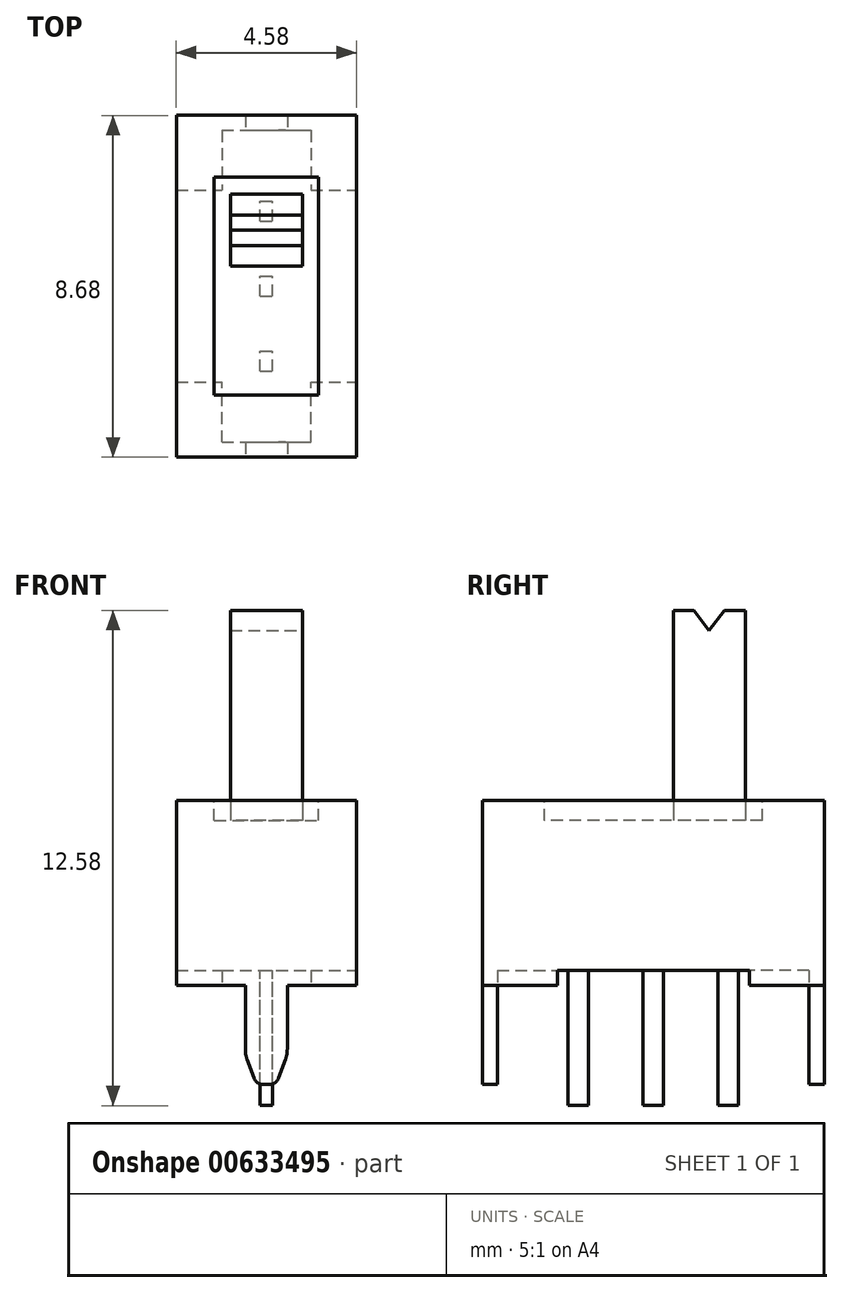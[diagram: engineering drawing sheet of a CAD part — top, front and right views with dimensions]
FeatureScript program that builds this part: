
annotation { "Feature Type Name" : "Feature", "Feature Type Description" : "" }
export const myFeature = defineFeature(function(context is Context, id is Id, definition is map)
    precondition{}
    {
        {
            var Q0;
            Q0=qCreatedBy(makeId("Top.planeOp"),FACE);
            var sketch = newSketch(context, id + "F0", { "sketchPlane" : qUnion([Q0])});
            skLineSegment(sketch, "E0.bottom", {"start": v(2.29, 4.34) * mm, "end": v(-2.29, 4.34) * mm});
            skLineSegment(sketch, "E0.top", {"start": v(2.29, -4.34) * mm, "end": v(-2.29, -4.34) * mm});
            skLineSegment(sketch, "E0.left", {"start": v(2.29, 4.34) * mm, "end": v(2.29, -4.34) * mm});
            skLineSegment(sketch, "E0.right", {"start": v(-2.29, 4.34) * mm, "end": v(-2.29, -4.34) * mm});
            skLineSegment(sketch, "E1", {"start": v(2.29, 4.34) * mm, "end": v(-2.29, -4.34) * mm, "construction": true});
            skSolve(sketch);
        }
        {
            var Q0;
            Q0 = qSketchRegion(id + "F0", true);
            var Q1;
            Q1=makeQuery(id+"F0.imprint","IMPRINT",FACE,{"disambiguationData":[TD([[makeQuery(id+"F0.imprint","IMPRINT",EDGE,{"derivedFrom":sQuery(id+"F0.wireOp",EDGE,"E0.bottom")}),1.0]])]});
            extrude(context, id + "F1", {"entities" : qUnion([Q0, Q1]), "endBound" : BoundingType.SYMMETRIC, "depth" : 4.7 * mm, "offsetDistance" : 25.4 * mm});
        }
        {
            var Q0;
            Q0=makeQuery(id+"F1.opExtrude","CAP_FACE",FACE,{"disambiguationData":[OSD([sQuery(id+"F0.wireOp",EDGE,"E0.bottom"),sQuery(id+"F0.wireOp",EDGE,"E0.top"),sQuery(id+"F0.wireOp",EDGE,"E0.left"),sQuery(id+"F0.wireOp",EDGE,"E0.right")])],"isStart":false});
            var sketch = newSketch(context, id + "F2", { "sketchPlane" : qUnion([Q0])});
            skLineSegment(sketch, "E2.bottom", {"start": v(-1.32, 2.77) * mm, "end": v(1.32, 2.77) * mm});
            skLineSegment(sketch, "E2.top", {"start": v(-1.32, -2.77) * mm, "end": v(1.32, -2.77) * mm});
            skLineSegment(sketch, "E2.left", {"start": v(-1.32, 2.77) * mm, "end": v(-1.32, -2.77) * mm});
            skLineSegment(sketch, "E2.right", {"start": v(1.32, 2.77) * mm, "end": v(1.32, -2.77) * mm});
            skLineSegment(sketch, "E3", {"start": v(1.32, 2.77) * mm, "end": v(-1.32, -2.77) * mm, "construction": true});
            skSolve(sketch);
        }
        {
            var Q0;
            Q0 = qSketchRegion(id + "F2", true);
            extrude(context, id + "F3", {"entities" : qUnion([Q0]), "operationType" : NewBodyOperationType.REMOVE, "oppositeDirection" : true, "depth" : 0.5 * mm, "offsetDistance" : 25.4 * mm});
        }
        {
            var Q0;
            Q0=makeQuery(id+"F1.opExtrude","CAP_FACE",FACE,{"disambiguationData":[OSD([sQuery(id+"F0.wireOp",EDGE,"E0.bottom"),sQuery(id+"F0.wireOp",EDGE,"E0.top"),sQuery(id+"F0.wireOp",EDGE,"E0.left"),sQuery(id+"F0.wireOp",EDGE,"E0.right")])],"isStart":true});
            var sketch = newSketch(context, id + "F4", { "sketchPlane" : qUnion([Q0])});
            skLineSegment(sketch, "E4.bottom", {"start": v(-0.91, -0.5) * mm, "end": v(0.91, -0.5) * mm});
            skLineSegment(sketch, "E4.top", {"start": v(-0.91, -2.34) * mm, "end": v(0.91, -2.34) * mm});
            skLineSegment(sketch, "E4.left", {"start": v(-0.91, -0.5) * mm, "end": v(-0.91, -2.34) * mm});
            skLineSegment(sketch, "E4.right", {"start": v(0.91, -0.5) * mm, "end": v(0.91, -2.34) * mm});
            skLineSegment(sketch, "E5", {"start": v(0, 0) * mm, "end": v(0, -0.5) * mm, "construction": true});
            skSolve(sketch);
        }
        {
            var Q0;
            Q0 = qSketchRegion(id + "F4", true);
            extrude(context, id + "F5", {"entities" : qUnion([Q0]), "operationType" : NewBodyOperationType.ADD, "oppositeDirection" : true, "depth" : 9.52 * mm, "offsetDistance" : 25.4 * mm});
        }
        {
            var Q0;
            Q0=qCreatedBy(makeId("Right.planeOp"),FACE);
            var sketch = newSketch(context, id + "F6", { "sketchPlane" : qUnion([Q0])});
            skLineSegment(sketch, "E6", {"start": v(1.42, 7.18) * mm, "end": v(1.42, 13.06) * mm, "construction": true});
            skLineSegment(sketch, "E7", {"start": v(1.03, 7.18) * mm, "end": v(1.81, 7.18) * mm});
            skLineSegment(sketch, "E8", {"start": v(1.81, 7.18) * mm, "end": v(1.42, 6.67) * mm});
            skLineSegment(sketch, "E9", {"start": v(1.42, 6.67) * mm, "end": v(1.03, 7.18) * mm});
            skSolve(sketch);
        }
        {
            var Q0;
            Q0 = qSketchRegion(id + "F6", true);
            extrude(context, id + "F7", {"entities" : qUnion([Q0]), "operationType" : NewBodyOperationType.REMOVE, "endBound" : BoundingType.SYMMETRIC, "oppositeDirection" : true, "depth" : 25.4 * mm, "offsetDistance" : 25.4 * mm});
        }
        {
            var Q0;
            Q0=makeQuery(id+"F1.opExtrude","CAP_FACE",FACE,{"disambiguationData":[OSD([sQuery(id+"F0.wireOp",EDGE,"E0.bottom"),sQuery(id+"F0.wireOp",EDGE,"E0.top"),sQuery(id+"F0.wireOp",EDGE,"E0.left"),sQuery(id+"F0.wireOp",EDGE,"E0.right")])],"isStart":true});
            var sketch = newSketch(context, id + "F8", { "sketchPlane" : qUnion([Q0])});
            skLineSegment(sketch, "E10", {"start": v(-1.82, 0) * mm, "end": v(7.05, 0) * mm, "construction": true});
            skLineSegment(sketch, "E11.bottom", {"start": v(-1.13, 3.96) * mm, "end": v(1.13, 3.96) * mm});
            skLineSegment(sketch, "E11.left", {"start": v(-1.13, 3.96) * mm, "end": v(-1.13, 2.44) * mm});
            skLineSegment(sketch, "E11.right", {"start": v(1.13, 3.96) * mm, "end": v(1.13, 2.44) * mm});
            skLineSegment(sketch, "E12.bottom", {"start": v(-2.29, 2.44) * mm, "end": v(-1.13, 2.44) * mm});
            skLineSegment(sketch, "E12.left", {"start": v(-2.29, 2.44) * mm, "end": v(-2.29, 0) * mm});
            skLineSegment(sketch, "E12.right", {"start": v(2.29, 2.44) * mm, "end": v(2.29, 0) * mm});
            skLineSegment(sketch, "E13.trimOffspring", {"start": v(1.13, 2.44) * mm, "end": v(2.29, 2.44) * mm});
            skLineSegment(sketch, "E14", {"start": v(0, 0) * mm, "end": v(0, 6.83) * mm, "construction": true});
            skLineSegment(sketch, "E15.MirrorCS", {"start": v(-2.29, -2.44) * mm, "end": v(-2.29, 0) * mm});
            skLineSegment(sketch, "E16.MirrorCS", {"start": v(-2.29, -2.44) * mm, "end": v(-1.13, -2.44) * mm});
            skLineSegment(sketch, "E17.MirrorCS", {"start": v(1.13, -3.96) * mm, "end": v(1.13, -2.44) * mm});
            skLineSegment(sketch, "E18.MirrorCS", {"start": v(-1.13, -3.96) * mm, "end": v(-1.13, -2.44) * mm});
            skLineSegment(sketch, "E19.MirrorCS", {"start": v(-1.13, -3.96) * mm, "end": v(1.13, -3.96) * mm});
            skLineSegment(sketch, "E20.MirrorCS", {"start": v(1.13, -2.44) * mm, "end": v(2.29, -2.44) * mm});
            skLineSegment(sketch, "E21.MirrorCS", {"start": v(2.29, -2.44) * mm, "end": v(2.29, 0) * mm});
            skSolve(sketch);
        }
        {
            var Q0;
            Q0 = qSketchRegion(id + "F8", true);
            extrude(context, id + "F9", {"entities" : qUnion([Q0]), "operationType" : NewBodyOperationType.REMOVE, "oppositeDirection" : true, "depth" : 0.38 * mm, "offsetDistance" : 25.4 * mm});
        }
        {
            var Q0;
            Q0=qCreatedBy(makeId("Front.planeOp"),FACE);
            var sketch = newSketch(context, id + "F10", { "sketchPlane" : qUnion([Q0])});
            skLineSegment(sketch, "E22.bottom", {"start": v(0.53, -2.35) * mm, "end": v(-0.53, -2.35) * mm});
            skLineSegment(sketch, "E22.top", {"start": v(0.08, -4.86) * mm, "end": v(-0.08, -4.86) * mm});
            skLineSegment(sketch, "E22.left", {"start": v(0.53, -2.35) * mm, "end": v(0.53, -3.97) * mm});
            skLineSegment(sketch, "E22.right", {"start": v(-0.53, -2.35) * mm, "end": v(-0.53, -3.97) * mm});
            skLineSegment(sketch, "E23", {"start": v(0, 0) * mm, "end": v(0, -2.35) * mm, "construction": true});
            skLineSegment(sketch, "E24", {"start": v(0.32, -4.7) * mm, "end": v(0.49, -4.23) * mm});
            skLineSegment(sketch, "E25.MirrorCS", {"start": v(-0.32, -4.7) * mm, "end": v(-0.49, -4.23) * mm});
            skPoint(sketch, "E26.orphan", {"position": v(-0.53, -4.86) * mm});
            skPoint(sketch, "E27.visualSharp", {"position": v(-0.53, -4.1) * mm});
            skArc(sketch, "E27.filletArc", {"start": v(-0.53, -3.97) * mm, "mid": v(-0.52, -4.1) * mm, "end": v(-0.49, -4.23) * mm});
            skPoint(sketch, "E28.visualSharp", {"position": v(-0.26, -4.86) * mm});
            skArc(sketch, "E28.filletArc", {"start": v(-0.32, -4.7) * mm, "mid": v(-0.22, -4.82) * mm, "end": v(-0.08, -4.86) * mm});
            skPoint(sketch, "E29.visualSharp", {"position": v(0.26, -4.86) * mm});
            skArc(sketch, "E29.filletArc", {"start": v(0.08, -4.86) * mm, "mid": v(0.22, -4.82) * mm, "end": v(0.32, -4.7) * mm});
            skPoint(sketch, "E30.visualSharp", {"position": v(0.53, -4.1) * mm});
            skArc(sketch, "E30.filletArc", {"start": v(0.49, -4.23) * mm, "mid": v(0.52, -4.1) * mm, "end": v(0.53, -3.97) * mm});
            skSolve(sketch);
        }
        {
            var Q0;
            Q0 = qSketchRegion(id + "F10", true);
            var Q1;
            Q1=makeQuery(id+"F1.opExtrude","SWEPT_FACE",FACE,{"disambiguationData":[OSD([sQuery(id+"F0.wireOp",EDGE,"E0.bottom")])]});
            var Q2;
            Q2=makeQuery(id+"F1.opExtrude","SWEPT_FACE",FACE,{"disambiguationData":[OSD([sQuery(id+"F0.wireOp",EDGE,"E0.top")])]});
            extrude(context, id + "F11", {"entities" : qUnion([Q0]), "operationType" : NewBodyOperationType.ADD, "endBound" : BoundingType.UP_TO_SURFACE, "oppositeDirection" : true, "depth" : 0.38 * mm, "endBoundEntityFace" : qUnion([Q1]), "offsetDistance" : 25.4 * mm, "hasSecondDirection" : true, "secondDirectionBound" : SecondDirectionBoundingType.UP_TO_SURFACE, "secondDirectionOppositeDirection" : false, "secondDirectionDepth" : 25.4 * mm, "secondDirectionBoundEntityFace" : qUnion([Q2])});
        }
        {
            var Q0;
            Q0=makeQuery(id+"F9.boolean.opBoolean","COPY",FACE,{"derivedFrom":makeQuery(id+"F9.opExtrude","CAP_FACE",FACE,{"disambiguationData":[OSD([sQuery(id+"F8.wireOp",EDGE,"E11.bottom"),sQuery(id+"F8.wireOp",EDGE,"E11.left"),sQuery(id+"F8.wireOp",EDGE,"E11.right"),sQuery(id+"F8.wireOp",EDGE,"E12.bottom"),sQuery(id+"F8.wireOp",EDGE,"E12.left"),sQuery(id+"F8.wireOp",EDGE,"E12.right"),sQuery(id+"F8.wireOp",EDGE,"E13.trimOffspring"),sQuery(id+"F8.wireOp",EDGE,"E15.MirrorCS"),sQuery(id+"F8.wireOp",EDGE,"E16.MirrorCS"),sQuery(id+"F8.wireOp",EDGE,"E17.MirrorCS"),sQuery(id+"F8.wireOp",EDGE,"E18.MirrorCS"),sQuery(id+"F8.wireOp",EDGE,"E19.MirrorCS"),sQuery(id+"F8.wireOp",EDGE,"E20.MirrorCS"),sQuery(id+"F8.wireOp",EDGE,"E21.MirrorCS")])],"isStart":false})});
            var sketch = newSketch(context, id + "F12", { "sketchPlane" : qUnion([Q0])});
            skLineSegment(sketch, "E31.bottom", {"start": v(1.13, 3.96) * mm, "end": v(-1.13, 3.96) * mm});
            skLineSegment(sketch, "E31.top", {"start": v(1.13, -3.96) * mm, "end": v(-1.13, -3.96) * mm});
            skLineSegment(sketch, "E31.left", {"start": v(1.13, 3.96) * mm, "end": v(1.13, -3.96) * mm});
            skLineSegment(sketch, "E31.right", {"start": v(-1.13, 3.96) * mm, "end": v(-1.13, -3.96) * mm});
            skSolve(sketch);
        }
        {
            var Q0;
            Q0 = qSketchRegion(id + "F12", true);
            extrude(context, id + "F13", {"entities" : qUnion([Q0]), "operationType" : NewBodyOperationType.REMOVE, "endBound" : BoundingType.THROUGH_ALL, "depth" : 25.4 * mm, "offsetDistance" : 25.4 * mm});
        }
        {
            var Q0;
            Q0=makeQuery(id+"F9.boolean.opBoolean","COPY",FACE,{"derivedFrom":makeQuery(id+"F9.opExtrude","CAP_FACE",FACE,{"disambiguationData":[OSD([sQuery(id+"F8.wireOp",EDGE,"E11.bottom"),sQuery(id+"F8.wireOp",EDGE,"E11.left"),sQuery(id+"F8.wireOp",EDGE,"E11.right"),sQuery(id+"F8.wireOp",EDGE,"E12.bottom"),sQuery(id+"F8.wireOp",EDGE,"E12.left"),sQuery(id+"F8.wireOp",EDGE,"E12.right"),sQuery(id+"F8.wireOp",EDGE,"E13.trimOffspring"),sQuery(id+"F8.wireOp",EDGE,"E15.MirrorCS"),sQuery(id+"F8.wireOp",EDGE,"E16.MirrorCS"),sQuery(id+"F8.wireOp",EDGE,"E17.MirrorCS"),sQuery(id+"F8.wireOp",EDGE,"E18.MirrorCS"),sQuery(id+"F8.wireOp",EDGE,"E19.MirrorCS"),sQuery(id+"F8.wireOp",EDGE,"E20.MirrorCS"),sQuery(id+"F8.wireOp",EDGE,"E21.MirrorCS")])],"isStart":false})});
            var sketch = newSketch(context, id + "F14", { "sketchPlane" : qUnion([Q0])});
            skLineSegment(sketch, "E32.bottom", {"start": v(-0.15, 2.16) * mm, "end": v(0.15, 2.16) * mm});
            skLineSegment(sketch, "E32.top", {"start": v(-0.15, 1.65) * mm, "end": v(0.15, 1.65) * mm});
            skLineSegment(sketch, "E32.left", {"start": v(-0.15, 2.16) * mm, "end": v(-0.15, 1.65) * mm});
            skLineSegment(sketch, "E32.right", {"start": v(0.15, 2.16) * mm, "end": v(0.15, 1.65) * mm});
            skLineSegment(sketch, "E33", {"start": v(0, 2.16) * mm, "end": v(0, -3.4) * mm, "construction": true});
            skLineSegment(sketch, "E34.1.0.0", {"start": v(0.15, 0.25) * mm, "end": v(0.15, -0.25) * mm});
            skLineSegment(sketch, "E34.1.0.1", {"start": v(-0.15, 0.25) * mm, "end": v(0.15, 0.25) * mm});
            skLineSegment(sketch, "E34.1.0.2", {"start": v(-0.15, -0.25) * mm, "end": v(0.15, -0.25) * mm});
            skLineSegment(sketch, "E34.1.0.3", {"start": v(-0.15, 0.25) * mm, "end": v(-0.15, -0.25) * mm});
            skLineSegment(sketch, "E34.2.0.0", {"start": v(0.15, -1.65) * mm, "end": v(0.15, -2.16) * mm});
            skLineSegment(sketch, "E34.2.0.1", {"start": v(-0.15, -1.65) * mm, "end": v(0.15, -1.65) * mm});
            skLineSegment(sketch, "E34.2.0.2", {"start": v(-0.15, -2.16) * mm, "end": v(0.15, -2.16) * mm});
            skLineSegment(sketch, "E34.2.0.3", {"start": v(-0.15, -1.65) * mm, "end": v(-0.15, -2.16) * mm});
            skLineSegment(sketch, "E34.direction1", {"start": v(-0.15, 1.65) * mm, "end": v(-0.15, -0.25) * mm, "construction": true});
            skLineSegment(sketch, "E35", {"start": v(0.15, 0.25) * mm, "end": v(-0.15, -0.25) * mm, "construction": true});
            skLineSegment(sketch, "E36", {"start": v(0.15, -1.65) * mm, "end": v(-0.15, -2.16) * mm, "construction": true});
            skSolve(sketch);
        }
        {
            var Q0;
            Q0 = qSketchRegion(id + "F14", true);
            extrude(context, id + "F15", {"entities" : qUnion([Q0]), "operationType" : NewBodyOperationType.ADD, "depth" : 3.43 * mm, "offsetDistance" : 25.4 * mm});
        }
    });
